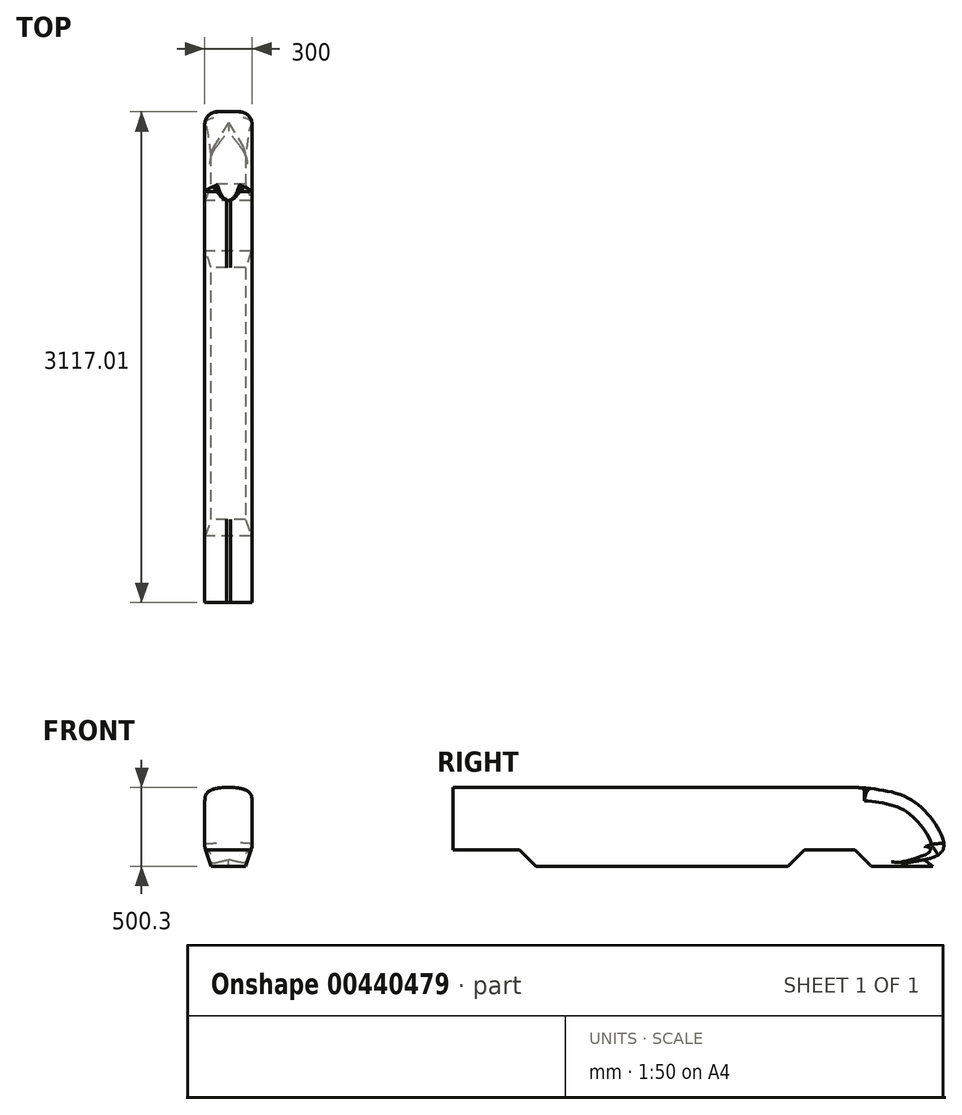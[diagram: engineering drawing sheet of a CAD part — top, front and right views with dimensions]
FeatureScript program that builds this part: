
annotation { "Feature Type Name" : "Feature", "Feature Type Description" : "" }
export const myFeature = defineFeature(function(context is Context, id is Id, definition is map)
    precondition{}
    {
        {
            var Q0;
            Q0=qCreatedBy(makeId("Right.planeOp"),FACE);
            var sketch = newSketch(context, id + "F0", { "sketchPlane" : qUnion([Q0])});
            skLineSegment(sketch, "E0.bottom", {"start": v(0, 525) * mm, "end": v(800, 525) * mm});
            skLineSegment(sketch, "E0.top", {"start": v(0, 25) * mm, "end": v(800, 25) * mm});
            skLineSegment(sketch, "E0.left", {"start": v(0, 525) * mm, "end": v(0, 25) * mm});
            skLineSegment(sketch, "E0.right", {"start": v(800, 525) * mm, "end": v(800, 25) * mm});
            skLineSegment(sketch, "E1", {"start": v(800, 25) * mm, "end": v(905, 130) * mm});
            skLineSegment(sketch, "E2", {"start": v(905, 130) * mm, "end": v(1225.81, 130) * mm});
            skLineSegment(sketch, "E3", {"start": v(1225.81, 130) * mm, "end": v(1225.81, 525.3) * mm});
            skLineSegment(sketch, "E4", {"start": v(1225.81, 525.3) * mm, "end": v(800, 525) * mm});
            skFitSpline(sketch, "E5", {"points": [v(1225.81, 525.3) * mm, v(1474.42, 491.92) * mm, v(1678.83, 367.83) * mm, v(1785.48, 130.05) * mm, v(1668.2, 66.75) * mm], "startDerivative": vector(736.9, -29.66) * mm, "endDerivative": vector(-500.47, -93.93) * mm});
            skLineSegment(sketch, "E6", {"start": v(1225.81, 130) * mm, "end": v(1330.81, 25) * mm});
            skLineSegment(sketch, "E7", {"start": v(1330.81, 25) * mm, "end": v(1720.72, 25) * mm});
            skLineSegment(sketch, "E8", {"start": v(1720.72, 25) * mm, "end": v(1668.2, 66.75) * mm});
            skSolve(sketch);
        }
        {
            var Q0;
            Q0=makeQuery(id+"F0.imprint","IMPRINT",FACE,{"disambiguationData":[TD([[makeQuery(id+"F0.imprint","IMPRINT",EDGE,{"derivedFrom":sQuery(id+"F0.wireOp",EDGE,"E0.right")}),1.0]])]});
            var Q1;
            Q1=makeQuery(id+"F0.imprint","IMPRINT",FACE,{"disambiguationData":[TD([[makeQuery(id+"F0.imprint","IMPRINT",EDGE,{"derivedFrom":sQuery(id+"F0.wireOp",EDGE,"E0.bottom")}),-1.0]])]});
            extrude(context, id + "F1", {"entities" : qUnion([Q0, Q1]), "depth" : 150 * mm});
        }
        {
            var Q0;
            Q0=makeQuery(id+"F1.opExtrude","SWEPT_BODY",BODY,{"disambiguationData":[OSD([sQuery(id+"F0.wireOp",EDGE,"E0.bottom"),sQuery(id+"F0.wireOp",EDGE,"E0.top"),sQuery(id+"F0.wireOp",EDGE,"E0.left"),sQuery(id+"F0.wireOp",EDGE,"E1"),sQuery(id+"F0.wireOp",EDGE,"E2"),sQuery(id+"F0.wireOp",EDGE,"E3"),sQuery(id+"F0.wireOp",EDGE,"E4")])]});
            var Q1;
            Q1=qCreatedBy(makeId("Front.planeOp"),FACE);
            mirror(context, id + "F2", {"operationType" : NewBodyOperationType.ADD, "entities" : qUnion([Q0]), "mirrorPlane" : qUnion([Q1])});
        }
        {
            var Q0;
            Q0=makeQuery(id+"F0.imprint","IMPRINT",FACE,{"disambiguationData":[TD([[makeQuery(id+"F0.imprint","IMPRINT",EDGE,{"derivedFrom":sQuery(id+"F0.wireOp",EDGE,"E3")}),-1.0]])]});
            extrude(context, id + "F3", {"entities" : qUnion([Q0]), "operationType" : NewBodyOperationType.ADD, "depth" : 150 * mm});
        }
        {
            var Q0;
            Q0=qCreatedBy(makeId("Front.planeOp"),FACE);
            var sketch = newSketch(context, id + "F4", { "sketchPlane" : qUnion([Q0])});
            skFitSpline(sketch, "E9", {"points": [v(12.47, 525) * mm, v(107.93, 509.35) * mm, v(138.15, 486.54) * mm, v(150, 441.37) * mm], "startDerivative": vector(315.28, 0) * mm, "endDerivative": vector(0, -194.94) * mm});
            skLineSegment(sketch, "E10", {"start": v(150, 441.37) * mm, "end": v(236.86, 441.37) * mm});
            skLineSegment(sketch, "E11", {"start": v(236.86, 441.37) * mm, "end": v(236.86, 562.93) * mm});
            skLineSegment(sketch, "E12", {"start": v(236.86, 562.93) * mm, "end": v(12.58, 562.93) * mm});
            skLineSegment(sketch, "E13", {"start": v(12.58, 562.93) * mm, "end": v(12.47, 525) * mm});
            skSolve(sketch);
        }
        {
            var Q0;
            {var subQ0=sQuery(id+"F4.wireOp",EDGE,"mfqcfveL-yIrt-t5j7-YIxb-R8Ssbw6cutj6");Q0=makeQuery(id+"F4.imprint","IMPRINT",FACE,{"disambiguationData":[TD([[makeQuery(id+"F4.imprint","IMPRINT",EDGE,{"derivedFrom":subQ0}),-1.0]])]});}
            var Q1;
            Q1=makeQuery(id+"F4.imprint","IMPRINT",FACE,{"disambiguationData":[TD([[makeQuery(id+"F4.imprint","IMPRINT",EDGE,{"derivedFrom":sQuery(id+"F4.wireOp",EDGE,"E9")}),1.0]])]});
            extrude(context, id + "F5", {"entities" : qUnion([Q0, Q1]), "operationType" : NewBodyOperationType.REMOVE, "endBound" : BoundingType.THROUGH_ALL, "oppositeDirection" : true, "depth" : 25 * mm});
        }
        {
            var Q0;
            Q0=makeQuery(id+"F3.opExtrude","CAP_EDGE",EDGE,{"disambiguationData":[OSD([sQuery(id+"F0.wireOp",EDGE,"E5")])],"isStart":false});
            fillet(context, id + "F6", {"entities" : qUnion([Q0]), "radius" : 80 * mm, "tangentPropagation" : true, "allowEdgeOverflow" : false});
        }
        {
            var Q0;
            Q0=makeQuery(id+"F3.opExtrude","CAP_EDGE",EDGE,{"disambiguationData":[OSD([sQuery(id+"F0.wireOp",EDGE,"E8")])],"isStart":false});
            chamfer(context, id + "F7", {"entities" : qUnion([Q0]), "width" : 150 * mm, "tangentPropagation" : true});
        }
        {
            var Q0;
            Q0=makeQuery(id+"F2.opPattern","COPY",FACE,{"derivedFrom":makeQuery(id+"F1.opExtrude","SWEPT_FACE",FACE,{"disambiguationData":[OSD([sQuery(id+"F0.wireOp",EDGE,"E3")])]}),"instanceName":"1"});
            extrude(context, id + "F8", {"entities" : qUnion([Q0]), "operationType" : NewBodyOperationType.ADD, "depth" : 100 * mm});
        }
        {
            var Q0;
            Q0=makeQuery(id+"F4.imprint","IMPRINT",FACE,{"disambiguationData":[TD([[makeQuery(id+"F4.imprint","IMPRINT",EDGE,{"derivedFrom":sQuery(id+"F4.wireOp",EDGE,"E9")}),1.0]])]});
            extrude(context, id + "F9", {"entities" : qUnion([Q0]), "operationType" : NewBodyOperationType.REMOVE, "endBound" : BoundingType.THROUGH_ALL, "depth" : 25 * mm});
        }
        {
            var Q0;
            Q0=makeQuery(id+"F1.opExtrude","SWEPT_BODY",BODY,{"disambiguationData":[OSD([sQuery(id+"F0.wireOp",EDGE,"E0.bottom"),sQuery(id+"F0.wireOp",EDGE,"E0.top"),sQuery(id+"F0.wireOp",EDGE,"E0.left"),sQuery(id+"F0.wireOp",EDGE,"E1"),sQuery(id+"F0.wireOp",EDGE,"E2"),sQuery(id+"F0.wireOp",EDGE,"E3"),sQuery(id+"F0.wireOp",EDGE,"E4")])]});
            var Q1;
            Q1=qCreatedBy(makeId("Right.planeOp"),FACE);
            mirror(context, id + "F10", {"operationType" : NewBodyOperationType.ADD, "entities" : qUnion([Q0]), "mirrorPlane" : qUnion([Q1])});
        }
        {
            var Q0;
            {var subQ0=makeQuery(id+"F1.opExtrude","CAP_EDGE",EDGE,{"disambiguationData":[OSD([sQuery(id+"F0.wireOp",EDGE,"E0.top")])],"isStart":false});Q0=makeQuery(id+"F2.boolean.opBoolean","MERGE",EDGE,{"derivedFrom":[subQ0,makeQuery(id+"F2.opPattern","COPY",EDGE,{"derivedFrom":subQ0,"instanceName":"1"})]});}
            var Q1;
            {var subQ0=makeQuery(id+"F1.opExtrude","CAP_EDGE",EDGE,{"disambiguationData":[OSD([sQuery(id+"F0.wireOp",EDGE,"E0.top")])],"isStart":false});Q1=makeQuery(id+"F10.opPattern","COPY",EDGE,{"derivedFrom":makeQuery(id+"F2.boolean.opBoolean","MERGE",EDGE,{"derivedFrom":[subQ0,makeQuery(id+"F2.opPattern","COPY",EDGE,{"derivedFrom":subQ0,"instanceName":"1"})]}),"instanceName":"1"});}
            chamfer(context, id + "F11", {"entities" : qUnion([Q0, Q1]), "chamferType" : ChamferType.TWO_OFFSETS, "width1" : 40 * mm, "oppositeDirection" : true, "width2" : 120 * mm, "tangentPropagation" : true});
        }
        {
            var Q0;
            {var subQ0=makeQuery(id+"F1.opExtrude","CAP_EDGE",EDGE,{"disambiguationData":[OSD([sQuery(id+"F0.wireOp",EDGE,"E0.top")])],"isStart":false});Q0=makeQuery(id+"F11.opChamfer","BLEND_EDGE",EDGE,{"blendedFrom":[makeQuery(id+"F10.opPattern","COPY",EDGE,{"derivedFrom":makeQuery(id+"F2.boolean.opBoolean","MERGE",EDGE,{"derivedFrom":[subQ0,makeQuery(id+"F2.opPattern","COPY",EDGE,{"derivedFrom":subQ0,"instanceName":"1"})]}),"instanceName":"1"}),makeQuery(id+"F10.opPattern","COPY",FACE,{"derivedFrom":makeQuery(id+"F6.opFillet","BLEND_FACE",FACE,{"disambiguationData":[OSD([sQuery(id+"F0.wireOp",EDGE,"E5")])]}),"instanceName":"1"})],"blendedInto":[makeQuery(id+"F10.opPattern","COPY",FACE,{"derivedFrom":makeQuery(id+"F6.opFillet","BLEND_FACE",FACE,{"disambiguationData":[OSD([sQuery(id+"F0.wireOp",EDGE,"E5")])]}),"instanceName":"1"})]});}
            var Q1;
            {var subQ0=makeQuery(id+"F1.opExtrude","CAP_EDGE",EDGE,{"disambiguationData":[OSD([sQuery(id+"F0.wireOp",EDGE,"E0.top")])],"isStart":false});Q1=makeQuery(id+"F11.opChamfer","BLEND_EDGE",EDGE,{"blendedFrom":[makeQuery(id+"F10.opPattern","COPY",EDGE,{"derivedFrom":makeQuery(id+"F2.boolean.opBoolean","MERGE",EDGE,{"derivedFrom":[subQ0,makeQuery(id+"F2.opPattern","COPY",EDGE,{"derivedFrom":subQ0,"instanceName":"1"})]}),"instanceName":"1"}),makeQuery(id+"F10.opPattern","COPY",FACE,{"derivedFrom":makeQuery(id+"F7.opChamfer","BLEND_FACE",FACE,{"disambiguationData":[OSD([sQuery(id+"F0.wireOp",EDGE,"E8")])]}),"instanceName":"1"})],"blendedInto":[makeQuery(id+"F10.opPattern","COPY",FACE,{"derivedFrom":makeQuery(id+"F7.opChamfer","BLEND_FACE",FACE,{"disambiguationData":[OSD([sQuery(id+"F0.wireOp",EDGE,"E8")])]}),"instanceName":"1"})]});}
            var Q2;
            {var subQ0=makeQuery(id+"F1.opExtrude","CAP_EDGE",EDGE,{"disambiguationData":[OSD([sQuery(id+"F0.wireOp",EDGE,"E0.top")])],"isStart":false});Q2=makeQuery(id+"F11.opChamfer","BLEND_EDGE",EDGE,{"blendedFrom":[makeQuery(id+"F2.boolean.opBoolean","MERGE",EDGE,{"derivedFrom":[subQ0,makeQuery(id+"F2.opPattern","COPY",EDGE,{"derivedFrom":subQ0,"instanceName":"1"})]}),makeQuery(id+"F7.opChamfer","BLEND_FACE",FACE,{"disambiguationData":[OSD([sQuery(id+"F0.wireOp",EDGE,"E8")])]})],"blendedInto":[makeQuery(id+"F7.opChamfer","BLEND_FACE",FACE,{"disambiguationData":[OSD([sQuery(id+"F0.wireOp",EDGE,"E8")])]})]});}
            var Q3;
            {var subQ0=makeQuery(id+"F1.opExtrude","CAP_EDGE",EDGE,{"disambiguationData":[OSD([sQuery(id+"F0.wireOp",EDGE,"E0.top")])],"isStart":false});Q3=makeQuery(id+"F11.opChamfer","BLEND_EDGE",EDGE,{"blendedFrom":[makeQuery(id+"F2.boolean.opBoolean","MERGE",EDGE,{"derivedFrom":[subQ0,makeQuery(id+"F2.opPattern","COPY",EDGE,{"derivedFrom":subQ0,"instanceName":"1"})]}),makeQuery(id+"F6.opFillet","BLEND_FACE",FACE,{"disambiguationData":[OSD([sQuery(id+"F0.wireOp",EDGE,"E5")])]})],"blendedInto":[makeQuery(id+"F6.opFillet","BLEND_FACE",FACE,{"disambiguationData":[OSD([sQuery(id+"F0.wireOp",EDGE,"E5")])]})]});}
            fillet(context, id + "F12", {"entities" : qUnion([Q0, Q1, Q2, Q3]), "radius" : 30 * mm, "tangentPropagation" : true, "allowEdgeOverflow" : false});
        }
    });
